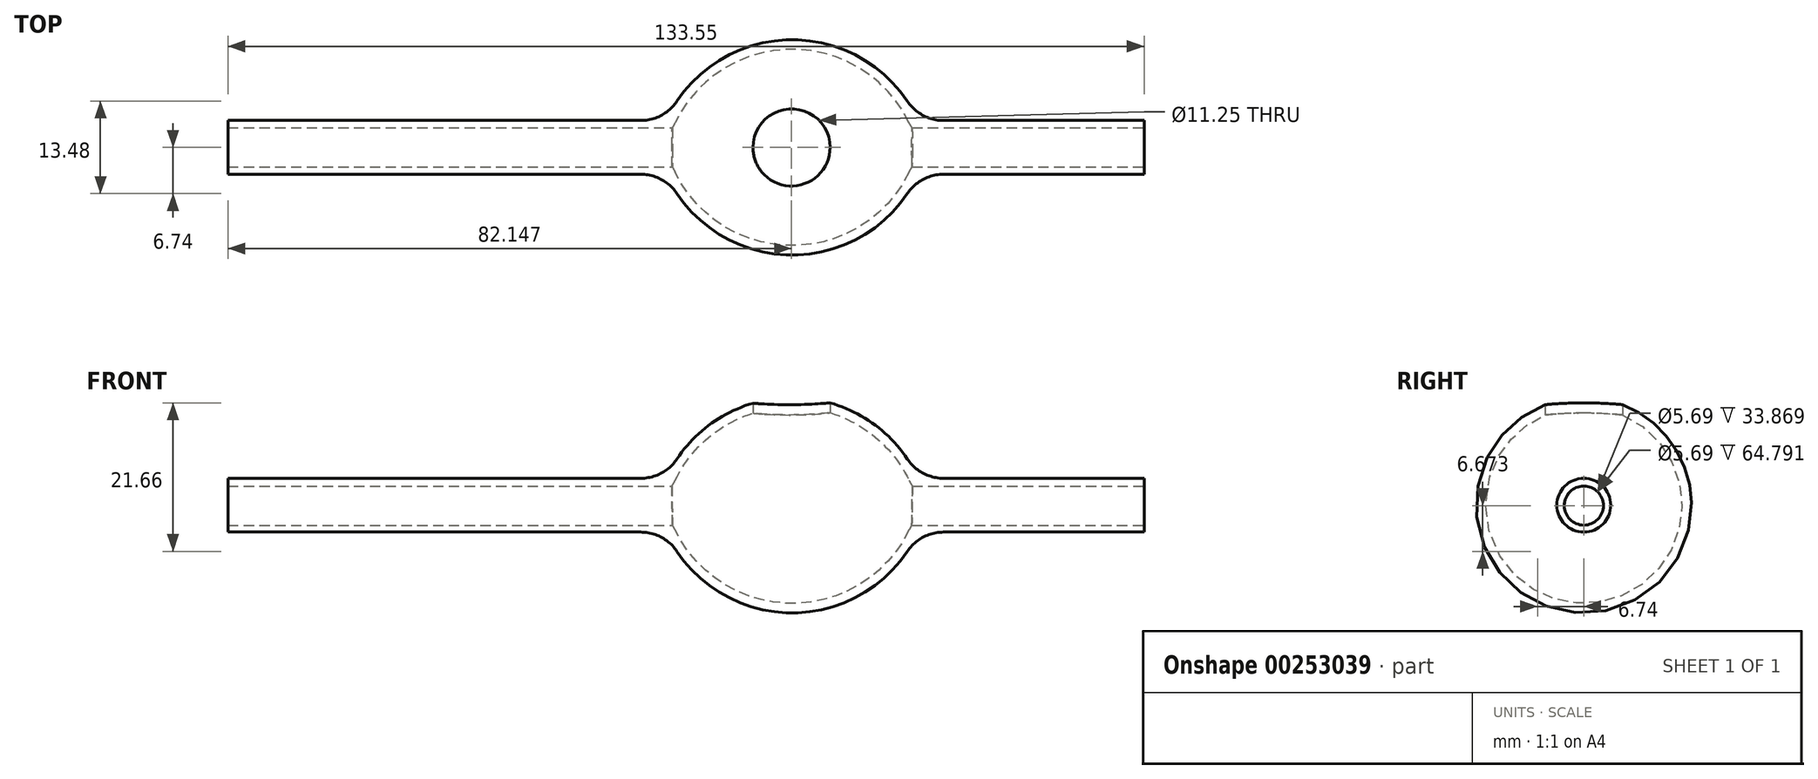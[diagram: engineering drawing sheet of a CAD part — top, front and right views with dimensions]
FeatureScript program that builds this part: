
annotation { "Feature Type Name" : "Feature", "Feature Type Description" : "" }
export const myFeature = defineFeature(function(context is Context, id is Id, definition is map)
    precondition{}
    {
        {
            var Q0;
            Q0=qCreatedBy(makeId("Front.planeOp"),FACE);
            var sketch = newSketch(context, id + "F0", { "sketchPlane" : qUnion([Q0])});
            skLineSegment(sketch, "E0.bottom", {"start": v(-63.87, 9.25) * mm, "end": v(-3.7, 9.25) * mm});
            skLineSegment(sketch, "E0.top", {"start": v(-63.87, 5.33) * mm, "end": v(-4.42, 5.33) * mm});
            skLineSegment(sketch, "E0.left", {"start": v(-63.87, 9.25) * mm, "end": v(-63.87, 5.33) * mm});
            skLineSegment(sketch, "E0.right", {"start": v(69.68, 9.25) * mm, "end": v(69.68, 5.33) * mm});
            skArc(sketch, "E1", {"start": v(35.16, 12.06) * mm, "mid": v(18.37, 21.02) * mm, "end": v(1.58, 12.06) * mm});
            skArc(sketch, "E2", {"start": v(35.43, 8.92) * mm, "mid": v(18.37, 19.63) * mm, "end": v(1.3, 8.92) * mm});
            skLineSegment(sketch, "E3.trimOffspring", {"start": v(40.43, 9.25) * mm, "end": v(69.68, 9.25) * mm});
            skLineSegment(sketch, "E4.trimOffspring", {"start": v(41.15, 5.33) * mm, "end": v(69.68, 5.33) * mm});
            skPoint(sketch, "E5.visualSharp", {"position": v(0, 9.25) * mm});
            skArc(sketch, "E5.filletArc", {"start": v(-3.7, 9.25) * mm, "mid": v(-0.7, 10) * mm, "end": v(1.58, 12.06) * mm});
            skPoint(sketch, "E6.visualSharp", {"position": v(36.73, 9.25) * mm});
            skArc(sketch, "E6.filletArc", {"start": v(35.16, 12.06) * mm, "mid": v(37.44, 10) * mm, "end": v(40.43, 9.25) * mm});
            skPoint(sketch, "E7.visualSharp", {"position": v(36.73, 5.33) * mm});
            skArc(sketch, "E7.filletArc", {"start": v(35.43, 8.92) * mm, "mid": v(37.77, 6.3) * mm, "end": v(41.15, 5.33) * mm});
            skPoint(sketch, "E8.visualSharp", {"position": v(0, 5.33) * mm});
            skArc(sketch, "E8.filletArc", {"start": v(-4.42, 5.33) * mm, "mid": v(-1.04, 6.3) * mm, "end": v(1.3, 8.92) * mm});
            skSolve(sketch);
        }
        {
            var Q0;
            Q0=makeQuery(id+"F0.imprint","IMPRINT",FACE,{"disambiguationData":[TD([[makeQuery(id+"F0.imprint","IMPRINT",EDGE,{"derivedFrom":sQuery(id+"F0.wireOp",EDGE,"E0.bottom")}),-1.0]])]});
            var Q1;
            Q1=sQuery(id+"F0.wireOp",EDGE,"E0.top");
            revolve(context, id + "F1", {"entities" : qUnion([Q0]), "axis" : qUnion([Q1]), "revolveType" : RevolveType.FULL});
        }
        {
            var Q0;
            Q0=makeQuery(id+"F1.opRevolve","SWEPT_FACE",FACE,{"disambiguationData":[OSD([sQuery(id+"F0.wireOp",EDGE,"E0.right")])]});
            var sketch = newSketch(context, id + "F2", { "sketchPlane" : qUnion([Q0])});
            skSolve(sketch);
        }
        {
            var Q0;
            Q0=makeQuery(id+"F2.imprint","IMPRINT",FACE,{"disambiguationData":[TD([[makeQuery(id+"F2.imprint","IMPRINT",EDGE,{"derivedFrom":makeQuery(id+"F1.opRevolve","SWEPT_EDGE",EDGE,{"disambiguationData":[OSD([sQuery(id+"F0.wireOp",EDGE,"E0.right"),sQuery(id+"F0.wireOp",EDGE,"E3.trimOffspring")])]})}),-1.0]])]});
            var sketch = newSketch(context, id + "F3", { "sketchPlane" : qUnion([Q0])});
            skCircle(sketch, "E9", {"center": v(0, 5.26) * mm, "radius": 2.85 * mm});
            skSolve(sketch);
        }
        {
            var Q0;
            Q0=makeQuery(id+"F3.imprint","IMPRINT",FACE,{"disambiguationData":[TD([[makeQuery(id+"F3.imprint","IMPRINT",EDGE,{"derivedFrom":sQuery(id+"F3.wireOp",EDGE,"E9")}),1.0]])]});
            var Q1;
            Q1=makeQuery(id+"F1.opRevolve","SWEPT_FACE",FACE,{"disambiguationData":[OSD([sQuery(id+"F0.wireOp",EDGE,"E0.left")])]});
            extrude(context, id + "F4", {"entities" : qUnion([Q0]), "operationType" : NewBodyOperationType.REMOVE, "endBound" : BoundingType.UP_TO_SURFACE, "oppositeDirection" : true, "endBoundEntityFace" : qUnion([Q1]), "depth" : 25.4 * mm});
        }
        {
            var Q0;
            Q0=qCreatedBy(makeId("Top.planeOp"),FACE);
            var sketch = newSketch(context, id + "F5", { "sketchPlane" : qUnion([Q0])});
            skCircle(sketch, "E10", {"center": v(18.28, 0) * mm, "radius": 5.63 * mm});
            skSolve(sketch);
        }
        {
            var Q0;
            Q0 = qSketchRegion(id + "F5", true);
            extrude(context, id + "F6", {"entities" : qUnion([Q0]), "operationType" : NewBodyOperationType.REMOVE, "depth" : 35.05 * mm});
        }
    });
